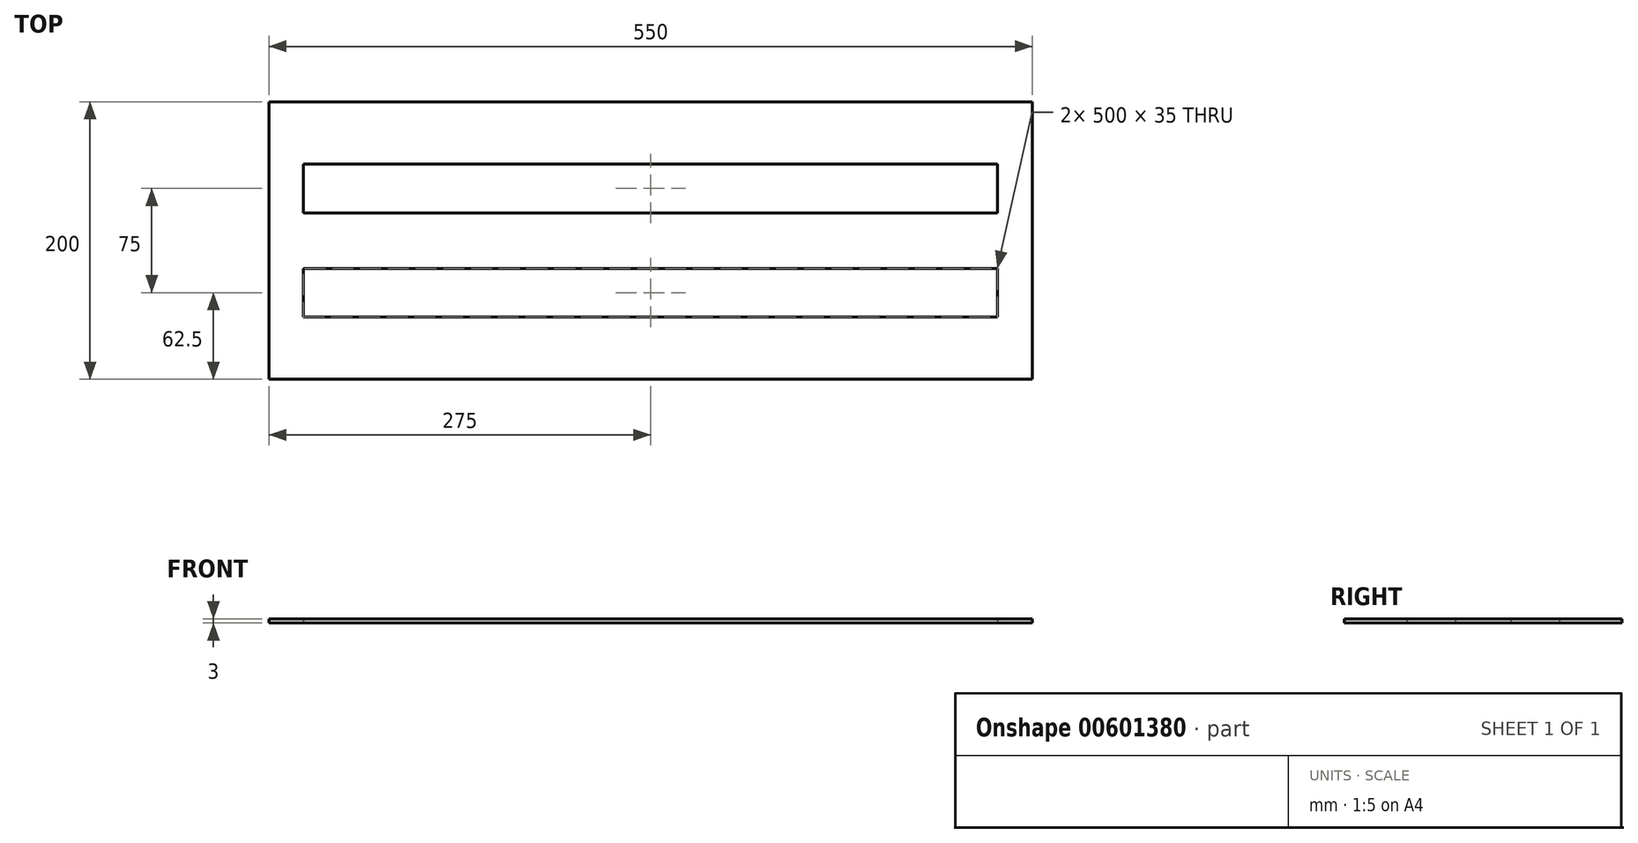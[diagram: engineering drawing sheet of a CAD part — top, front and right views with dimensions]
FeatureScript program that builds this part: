
annotation { "Feature Type Name" : "Feature", "Feature Type Description" : "" }
export const myFeature = defineFeature(function(context is Context, id is Id, definition is map)
    precondition{}
    {
        {
            var Q0;
            Q0=qCreatedBy(makeId("Top.planeOp"),FACE);
            var sketch = newSketch(context, id + "F0", { "sketchPlane" : qUnion([Q0])});
            skLineSegment(sketch, "E0.bottom", {"start": v(275, -100) * mm, "end": v(-275, -100) * mm});
            skLineSegment(sketch, "E0.top", {"start": v(275, 100) * mm, "end": v(-275, 100) * mm});
            skLineSegment(sketch, "E0.left", {"start": v(275, -100) * mm, "end": v(275, 100) * mm});
            skLineSegment(sketch, "E0.right", {"start": v(-275, -100) * mm, "end": v(-275, 100) * mm});
            skPoint(sketch, "E0.middle", {"position": v(0, 0) * mm});
            skLineSegment(sketch, "E1.bottom", {"start": v(250, 20) * mm, "end": v(-250, 20) * mm});
            skLineSegment(sketch, "E1.top", {"start": v(250, 55) * mm, "end": v(-250, 55) * mm});
            skLineSegment(sketch, "E1.left", {"start": v(250, 20) * mm, "end": v(250, 55) * mm});
            skLineSegment(sketch, "E1.right", {"start": v(-250, 20) * mm, "end": v(-250, 55) * mm});
            skPoint(sketch, "E1.middle", {"position": v(0, 37.5) * mm});
            skLineSegment(sketch, "E2.bottom", {"start": v(250, -55) * mm, "end": v(-250, -55) * mm});
            skLineSegment(sketch, "E2.top", {"start": v(250, -20) * mm, "end": v(-250, -20) * mm});
            skLineSegment(sketch, "E2.left", {"start": v(250, -55) * mm, "end": v(250, -20) * mm});
            skLineSegment(sketch, "E2.right", {"start": v(-250, -55) * mm, "end": v(-250, -20) * mm});
            skPoint(sketch, "E2.middle", {"position": v(0, -37.5) * mm});
            skSolve(sketch);
        }
        {
            var Q0;
            Q0 = qSketchRegion(id + "F0", true);
            extrude(context, id + "F1", {"entities" : qUnion([Q0]), "depth" : 3 * mm, "offsetDistance" : 25 * mm});
        }
    });
